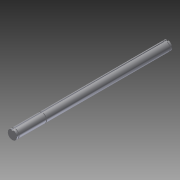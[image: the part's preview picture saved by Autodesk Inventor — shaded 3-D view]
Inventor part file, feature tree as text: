
AUTODESK INVENTOR PART (.ipt)
format: ipt  version: 2012 (Build 160160000, 160)  size: 112,128 bytes
history: native  units: in
note: dims shown in document units (in); Inventor stores cm internally (conversion verified against a paired STEP export)
features: extrude x4, sketch x4, plane x3, projected_geometry x1
ambient origin geometry x8: Origin, YZ Plane, XZ Plane, XY Plane, X Axis, Y Axis, Z Axis, Center Point
bodies: Solid1 (feature_tree)
feature tree (12):
  extrude  "Extrusion1"  Depth=6.375in TaperAngle=0.0deg
  plane  "Work Plane1"
  extrude  "Extrusion2"  Depth=0.0787in
  plane  "Work Plane2"
  extrude  "Extrusion3"  Depth=0.1481in
  plane  "Work Plane3"
  extrude  "Extrusion4"  Depth=0.03in
  sketch  "Sketch1"  dims[d0=0.375in d1=6.375in d2=0.0in]
  sketch  "Sketch2"  dims[d3=0.0787in d4=0.0787in]
  projected_geometry  "Projected Loop1"
  sketch  "Sketch3"  dims[d5=0.0394in d6=0.1481in]
  sketch  "Sketch4"  dims[d7=-0.0625in d9=0.03in d10=0.03in d11=0.0in d12=-5.145in d13=0.03in d14=0.0in d15=-0.0625in d16=0.04in d17=0.0in]
